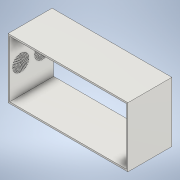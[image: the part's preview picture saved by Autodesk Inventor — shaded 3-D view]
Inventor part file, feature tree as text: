
AUTODESK INVENTOR PART (.ipt)
format: ipt  version: 2021 (Build 250183000, 183)  size: 763,392 bytes
history: native  units: mm
features: extrude x3, sketch x3, other x1, chamfer x1
ambient origin geometry x8: Origin, YZ Plane, XZ Plane, XY Plane, X Axis, Y Axis, Z Axis, Center Point
bodies: Body1 (feature_tree)
feature tree (8):
  other  "Sólido1"
  extrude  "Extrusão1"  Depth=600.0mm
  extrude  "Extrusão2"  Depth=284.0mm
  extrude  "Extrusão3"  Depth=2.0mm
  chamfer  "Chanfro1"  Distance=55.0mm
  sketch  "Esboço2"  dims[d0=300.0mm d1=600.0mm]
  sketch  "Esboço3"  dims[d2=584.0mm d3=284.0mm]
  sketch  "Esboço4"  dims[d4=220.0mm d5=0.0mm d8=150.0mm d11=55.0mm d15=10.0mm d17=10.0mm d18=90.0mm d20=5.0mm d22=50.0mm d24=360.0deg d26=100.0mm d28=360.0deg d30=150.0mm d32=360.0deg d34=200.0mm d36=360.0deg d38=250.0mm d40=360.0deg d42=300.0mm d44=360.0deg d46=350.0mm d48=360.0deg d50=400.0mm d52=360.0deg d54=10.0mm d55=0.0mm d56=500.0mm d57=292.0mm d58=4.0mm d59=4.0mm d60=4.0mm d61=4.0mm d62=4.0mm d63=4.0mm d64=30.0mm d65=0.0mm d66=1.0mm d67=2.0mm d68=45.0deg]
